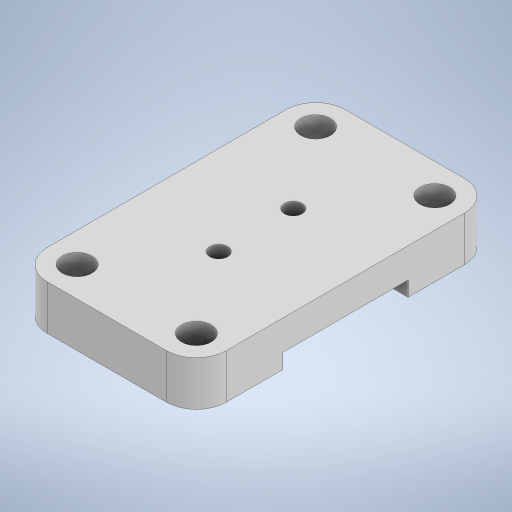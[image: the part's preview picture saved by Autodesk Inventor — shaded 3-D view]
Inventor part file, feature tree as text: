
AUTODESK INVENTOR PART (.ipt)
format: ipt  version: 2023.2 (Build 272271030, 271C)  size: 257,024 bytes
history: native  units: mm
features: extrude x2, sketch x2, fillet x1, projected_geometry x1
ambient origin geometry x8: Origin, YZ Plane, XZ Plane, XY Plane, X Axis, Y Axis, Z Axis, Center Point
bodies: Solid1 (feature_tree)
feature tree (6):
  extrude  "Extrusion1"  Depth=100.0mm
  fillet  "Fillet1"  Radius=10.0mm
  extrude  "Extrusion2"  Depth=5.0mm
  sketch  "Sketch1"  dims[d0=60.0mm d1=100.0mm d2=10.0mm]
  sketch  "Sketch2"  dims[d3=40.0mm d4=80.0mm d5=15.0mm d6=0.0mm d7=10.0mm d9=42.0mm d10=5.0mm d11=0.0mm d12=0.0mm d14=6.0mm d15=25.0mm d16=0.5mm d17=0.872665mm]
  projected_geometry  "Projected Loop1"
